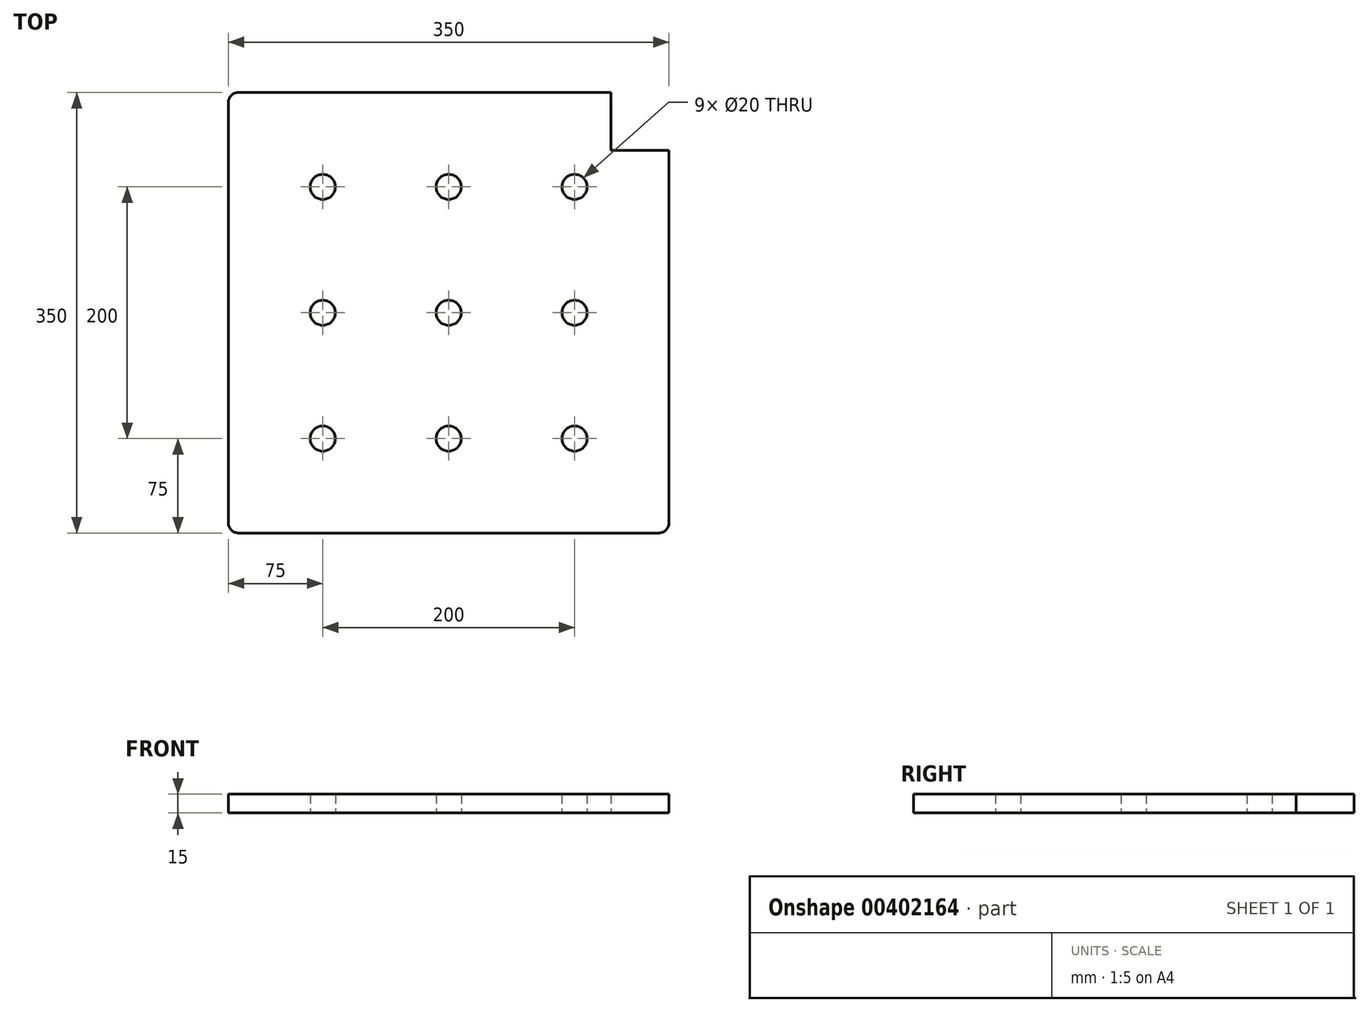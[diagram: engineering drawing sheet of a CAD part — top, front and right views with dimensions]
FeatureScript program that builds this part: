
annotation { "Feature Type Name" : "Feature", "Feature Type Description" : "" }
export const myFeature = defineFeature(function(context is Context, id is Id, definition is map)
    precondition{}
    {
        {
            var Q0;
            Q0=qCreatedBy(makeId("Top.planeOp"),FACE);
            var sketch = newSketch(context, id + "F0", { "sketchPlane" : qUnion([Q0])});
            skLineSegment(sketch, "E0.bottom", {"start": v(-167, 175) * mm, "end": v(129, 175) * mm});
            skLineSegment(sketch, "E0.top", {"start": v(-167, -175) * mm, "end": v(167, -175) * mm});
            skLineSegment(sketch, "E0.left", {"start": v(-175, 167) * mm, "end": v(-175, -167) * mm});
            skLineSegment(sketch, "E0.right", {"start": v(175, 129) * mm, "end": v(175, -167) * mm});
            skPoint(sketch, "E1.visualSharp", {"position": v(-175, 175) * mm});
            skArc(sketch, "E1.filletArc", {"start": v(-167, 175) * mm, "mid": v(-172.66, 172.66) * mm, "end": v(-175, 167) * mm});
            skPoint(sketch, "E2.visualSharp", {"position": v(-175, -175) * mm});
            skArc(sketch, "E2.filletArc", {"start": v(-175, -167) * mm, "mid": v(-172.66, -172.66) * mm, "end": v(-167, -175) * mm});
            skPoint(sketch, "E3.visualSharp", {"position": v(175, -175) * mm});
            skArc(sketch, "E3.filletArc", {"start": v(167, -175) * mm, "mid": v(172.66, -172.66) * mm, "end": v(175, -167) * mm});
            skCircle(sketch, "E4", {"center": v(-100, 100) * mm, "radius": 10 * mm});
            skCircle(sketch, "E5", {"center": v(0, 100) * mm, "radius": 10 * mm});
            skCircle(sketch, "E6", {"center": v(100, 100) * mm, "radius": 10 * mm});
            skCircle(sketch, "E7", {"center": v(-100, 0) * mm, "radius": 10 * mm});
            skCircle(sketch, "E8", {"center": v(0, 0) * mm, "radius": 10 * mm});
            skCircle(sketch, "E9", {"center": v(100, 0) * mm, "radius": 10 * mm});
            skCircle(sketch, "E10", {"center": v(-100, -100) * mm, "radius": 10 * mm});
            skCircle(sketch, "E11", {"center": v(0, -100) * mm, "radius": 10 * mm});
            skCircle(sketch, "E12", {"center": v(100, -100) * mm, "radius": 10 * mm});
            skLineSegment(sketch, "E13", {"start": v(129, 175) * mm, "end": v(129, 129) * mm});
            skLineSegment(sketch, "E14", {"start": v(129, 129) * mm, "end": v(175, 129) * mm});
            skSolve(sketch);
        }
        {
            var Q0;
            Q0 = qSketchRegion(id + "F0", true);
            extrude(context, id + "F1", {"entities" : qUnion([Q0]), "depth" : 15 * mm});
        }
    });
